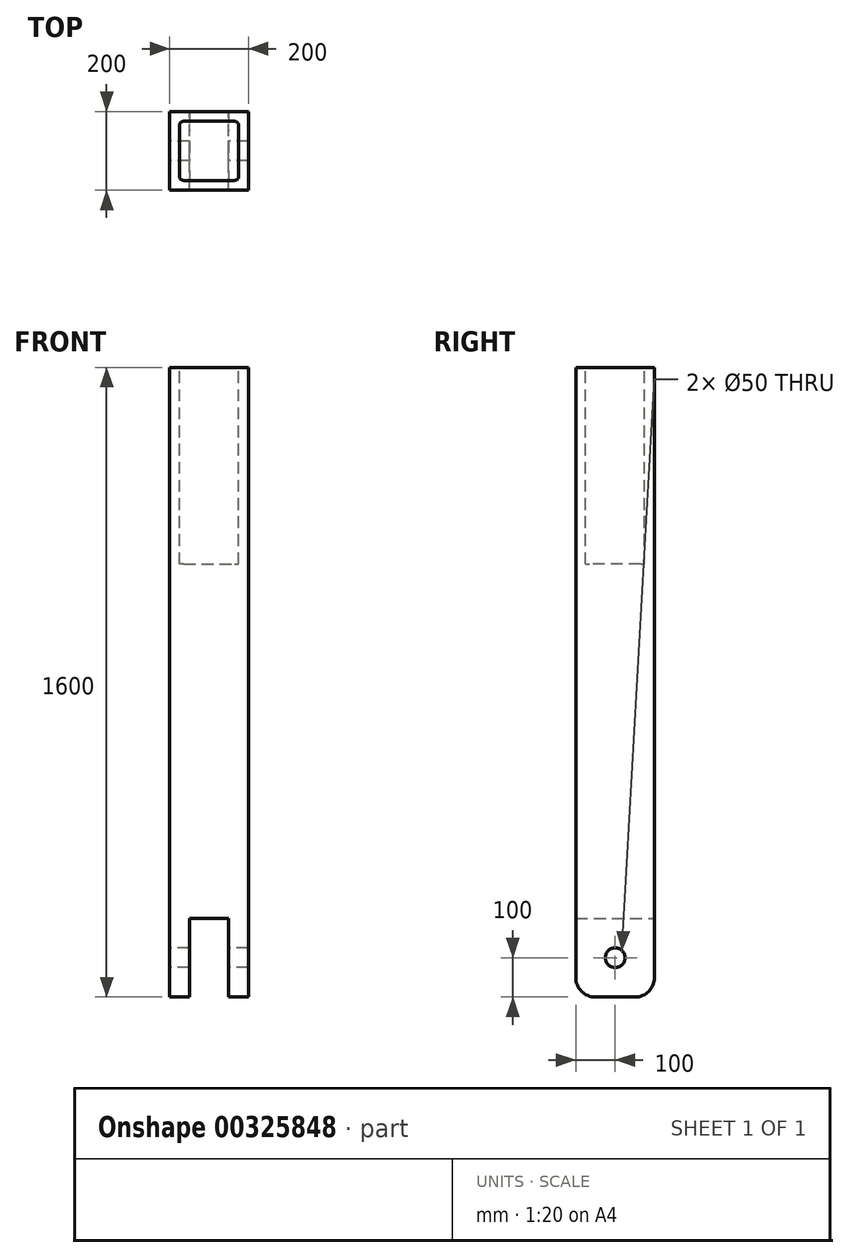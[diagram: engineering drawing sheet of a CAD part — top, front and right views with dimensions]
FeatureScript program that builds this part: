
annotation { "Feature Type Name" : "Feature", "Feature Type Description" : "" }
export const myFeature = defineFeature(function(context is Context, id is Id, definition is map)
    precondition{}
    {
        {
            var Q0;
            Q0=qCreatedBy(makeId("Right.planeOp"),FACE);
            var sketch = newSketch(context, id + "F0", { "sketchPlane" : qUnion([Q0])});
            skLineSegment(sketch, "E0.bottom", {"start": v(0, 0) * mm, "end": v(200, 0) * mm});
            skLineSegment(sketch, "E0.top", {"start": v(0, 1600) * mm, "end": v(200, 1600) * mm});
            skLineSegment(sketch, "E0.left", {"start": v(0, 0) * mm, "end": v(0, 1600) * mm});
            skLineSegment(sketch, "E0.right", {"start": v(200, 0) * mm, "end": v(200, 1600) * mm});
            skSolve(sketch);
        }
        {
            var Q0;
            Q0=makeQuery(id+"F0.imprint","IMPRINT",FACE,{"disambiguationData":[TD([[makeQuery(id+"F0.imprint","IMPRINT",EDGE,{"derivedFrom":sQuery(id+"F0.wireOp",EDGE,"E0.bottom")}),1.0]])]});
            var Q1;
            Q1=sQuery(id+"F0.wireOp",EDGE,"E0.left");
            var Q2;
            Q2=sQuery(id+"F0.wireOp",EDGE,"E0.right");
            var Q3;
            Q3=sQuery(id+"F0.wireOp",EDGE,"E0.bottom");
            var Q4;
            Q4=sQuery(id+"F0.wireOp",EDGE,"E0.top");
            extrude(context, id + "F1", {"entities" : qUnion([Q0]), "surfaceEntities" : qUnion([Q1, Q2, Q3, Q4]), "depth" : 200 * mm});
        }
        {
            var Q0;
            Q0=makeQuery(id+"F1.opExtrude","SWEPT_FACE",FACE,{"disambiguationData":[OSD([sQuery(id+"F0.wireOp",EDGE,"E0.right")])]});
            var sketch = newSketch(context, id + "F2", { "sketchPlane" : qUnion([Q0])});
            skLineSegment(sketch, "E1.bottom", {"start": v(-150, 0) * mm, "end": v(-50, 0) * mm});
            skLineSegment(sketch, "E1.top", {"start": v(-150, 200) * mm, "end": v(-50, 200) * mm});
            skLineSegment(sketch, "E1.left", {"start": v(-150, 0) * mm, "end": v(-150, 200) * mm});
            skLineSegment(sketch, "E1.right", {"start": v(-50, 0) * mm, "end": v(-50, 200) * mm});
            skSolve(sketch);
        }
        {
            var Q0;
            Q0=makeQuery(id+"F2.imprint","IMPRINT",FACE,{"disambiguationData":[TD([[makeQuery(id+"F2.imprint","IMPRINT",EDGE,{"derivedFrom":sQuery(id+"F2.wireOp",EDGE,"E1.bottom")}),1.0]])]});
            extrude(context, id + "F3", {"entities" : qUnion([Q0]), "operationType" : NewBodyOperationType.REMOVE, "oppositeDirection" : true, "depth" : 400 * mm});
        }
        {
            var Q0;
            Q0=makeQuery(id+"F1.opExtrude","SWEPT_FACE",FACE,{"disambiguationData":[OSD([sQuery(id+"F0.wireOp",EDGE,"E0.top")])]});
            var sketch = newSketch(context, id + "F4", { "sketchPlane" : qUnion([Q0])});
            skLineSegment(sketch, "E2.bottom", {"start": v(25, 175) * mm, "end": v(175, 175) * mm});
            skLineSegment(sketch, "E2.top", {"start": v(25, 25) * mm, "end": v(175, 25) * mm});
            skLineSegment(sketch, "E2.left", {"start": v(25, 175) * mm, "end": v(25, 25) * mm});
            skLineSegment(sketch, "E2.right", {"start": v(175, 175) * mm, "end": v(175, 25) * mm});
            skSolve(sketch);
        }
        {
            var Q0;
            Q0=makeQuery(id+"F4.imprint","IMPRINT",FACE,{"disambiguationData":[TD([[makeQuery(id+"F4.imprint","IMPRINT",EDGE,{"derivedFrom":sQuery(id+"F4.wireOp",EDGE,"E2.bottom")}),-1.0]])]});
            extrude(context, id + "F5", {"entities" : qUnion([Q0]), "operationType" : NewBodyOperationType.REMOVE, "oppositeDirection" : true, "depth" : 500 * mm});
        }
        {
            var Q0;
            Q0=makeQuery(id+"F1.opExtrude","CAP_FACE",FACE,{"disambiguationData":[OSD([sQuery(id+"F0.wireOp",EDGE,"E0.bottom"),sQuery(id+"F0.wireOp",EDGE,"E0.top"),sQuery(id+"F0.wireOp",EDGE,"E0.left"),sQuery(id+"F0.wireOp",EDGE,"E0.right")])],"isStart":true});
            var sketch = newSketch(context, id + "F6", { "sketchPlane" : qUnion([Q0])});
            skCircle(sketch, "E3", {"center": v(-100, 100) * mm, "radius": 25 * mm});
            skSolve(sketch);
        }
        {
            var Q0;
            Q0=makeQuery(id+"F6.imprint","IMPRINT",FACE,{"disambiguationData":[TD([[makeQuery(id+"F6.imprint","IMPRINT",EDGE,{"derivedFrom":sQuery(id+"F6.wireOp",EDGE,"E3")}),1.0]])]});
            extrude(context, id + "F7", {"entities" : qUnion([Q0]), "operationType" : NewBodyOperationType.REMOVE, "oppositeDirection" : true, "depth" : 300 * mm});
        }
        {
            var Q0;
            Q0=makeQuery(id+"F5.boolean.opBoolean","COPY",EDGE,{"derivedFrom":makeQuery(id+"F5.opExtrude","SWEPT_EDGE",EDGE,{"disambiguationData":[OSD([sQuery(id+"F4.wireOp",EDGE,"E2.bottom"),sQuery(id+"F4.wireOp",EDGE,"E2.left")])]})});
            var Q1;
            Q1=makeQuery(id+"F5.boolean.opBoolean","COPY",EDGE,{"derivedFrom":makeQuery(id+"F5.opExtrude","SWEPT_EDGE",EDGE,{"disambiguationData":[OSD([sQuery(id+"F4.wireOp",EDGE,"E2.bottom"),sQuery(id+"F4.wireOp",EDGE,"E2.right")])]})});
            var Q2;
            Q2=makeQuery(id+"F5.boolean.opBoolean","COPY",EDGE,{"derivedFrom":makeQuery(id+"F5.opExtrude","SWEPT_EDGE",EDGE,{"disambiguationData":[OSD([sQuery(id+"F4.wireOp",EDGE,"E2.top"),sQuery(id+"F4.wireOp",EDGE,"E2.left")])]})});
            var Q3;
            Q3=makeQuery(id+"F5.boolean.opBoolean","COPY",EDGE,{"derivedFrom":makeQuery(id+"F5.opExtrude","SWEPT_EDGE",EDGE,{"disambiguationData":[OSD([sQuery(id+"F4.wireOp",EDGE,"E2.top"),sQuery(id+"F4.wireOp",EDGE,"E2.right")])]})});
            fillet(context, id + "F8", {"entities" : qUnion([Q0, Q1, Q2, Q3]), "radius" : 10 * mm, "tangentPropagation" : true, "allowEdgeOverflow" : false});
        }
        {
            var Q0;
            {var subQ0=sQuery(id+"F0.wireOp",EDGE,"E0.bottom");var subQ1=sQuery(id+"F0.wireOp",EDGE,"E0.right");Q0=makeQuery(id+"F3.boolean.opBoolean","SPLIT",EDGE,{"disambiguationData":[TD([makeQuery(id+"F3.opExtrude","SWEPT_FACE",FACE,{"disambiguationData":[OSD([sQuery(id+"F2.wireOp",EDGE,"E1.left")])]})])],"derivedFrom":makeQuery(id+"F1.opExtrude","SWEPT_EDGE",EDGE,{"disambiguationData":[OSD([subQ0,subQ1])]})});}
            var Q1;
            {var subQ0=sQuery(id+"F0.wireOp",EDGE,"E0.bottom");var subQ1=sQuery(id+"F0.wireOp",EDGE,"E0.right");Q1=makeQuery(id+"F3.boolean.opBoolean","SPLIT",EDGE,{"disambiguationData":[TD([makeQuery(id+"F3.opExtrude","SWEPT_FACE",FACE,{"disambiguationData":[OSD([sQuery(id+"F2.wireOp",EDGE,"E1.right")])]})])],"derivedFrom":makeQuery(id+"F1.opExtrude","SWEPT_EDGE",EDGE,{"disambiguationData":[OSD([subQ0,subQ1])]})});}
            var Q2;
            {var subQ0=sQuery(id+"F0.wireOp",EDGE,"E0.bottom");var subQ1=sQuery(id+"F0.wireOp",EDGE,"E0.left");Q2=makeQuery(id+"F3.boolean.opBoolean","SPLIT",EDGE,{"disambiguationData":[TD([makeQuery(id+"F3.opExtrude","SWEPT_FACE",FACE,{"disambiguationData":[OSD([sQuery(id+"F2.wireOp",EDGE,"E1.left")])]})])],"derivedFrom":makeQuery(id+"F1.opExtrude","SWEPT_EDGE",EDGE,{"disambiguationData":[OSD([subQ0,subQ1])]})});}
            var Q3;
            {var subQ0=sQuery(id+"F0.wireOp",EDGE,"E0.bottom");var subQ1=sQuery(id+"F0.wireOp",EDGE,"E0.left");Q3=makeQuery(id+"F3.boolean.opBoolean","SPLIT",EDGE,{"disambiguationData":[TD([makeQuery(id+"F3.opExtrude","SWEPT_FACE",FACE,{"disambiguationData":[OSD([sQuery(id+"F2.wireOp",EDGE,"E1.right")])]})])],"derivedFrom":makeQuery(id+"F1.opExtrude","SWEPT_EDGE",EDGE,{"disambiguationData":[OSD([subQ0,subQ1])]})});}
            fillet(context, id + "F9", {"entities" : qUnion([Q0, Q1, Q2, Q3]), "radius" : 50 * mm, "tangentPropagation" : true, "allowEdgeOverflow" : false});
        }
    });
